# Revit family: Landscaping_Bike-Racks-Shelters_Saris-Infrastructure_Bike-Trac
name_source: partatom
category: Site
units: mm (PartAtom-declared; Revit-internal decimal feet)

## family parameters
Cut with Voids When Loaded = No
Host = Face
OmniClass Number = 23.40.10.11.11
OmniClass Title = Bicycle Racks
Part Type = Normal
Round Connector Dimension = Use Diameter
Shared = No

## types (2) — shared parameters
Default Elevation = 8.00 in
Length = 66.30 in
Manufacturer = Saris Infrastructure
Product Documentation Link = https://www.sarisinfrastructure.com
Product Material = Saris Infrastructure - Mild Steel - Powder Coat - Black
Product Page URL = https://www.sarisinfrastructure.com
Product Specifications = • Pivoting lock bar allows optimized locking position on all
bike frames and is shaped to prevent theft by use of a pipe
cutter
• Full length bike tracs protect walls and provide support for
both front and rear wheels for greater stability.
• Accommodates fat bikes tires up to 5” wide
• Tracs can be staggered in height to limit handlebar
interference between bikes
URL = https://www.sarisinfrastructure.com
Version = 1
Weight = 26.00 lb
Width = 6.50 in

## per-type parameters (varying)
| type | Description | Lock Bar | Model |
| Non-Locking Bike Trac | • Full length bike tracs protect walls and provide support for both front and rear wheels for greater stability. • Accommodates fat bikes tires up to 5” wide • Tracs can be staggered in height to limit handlebar interference between bikes | No | 6103 |
| Bike Trac w/ Locking Bar | • Pivoting lock bar allows optimized locking position on all bike frames and is shaped to prevent theft by use of a pipe cutter • Full length bike tracs protect walls and provide support for both front and rear wheels for greater stability. • Accommodates fat bikes tires up to 5” wide • Tracs can be staggered in height to limit handlebar interference between bikes | Yes | 6106 |

## geometry (parser evidence)
native form markers: Sweep x4
no freeform markers — native parametric forms only
